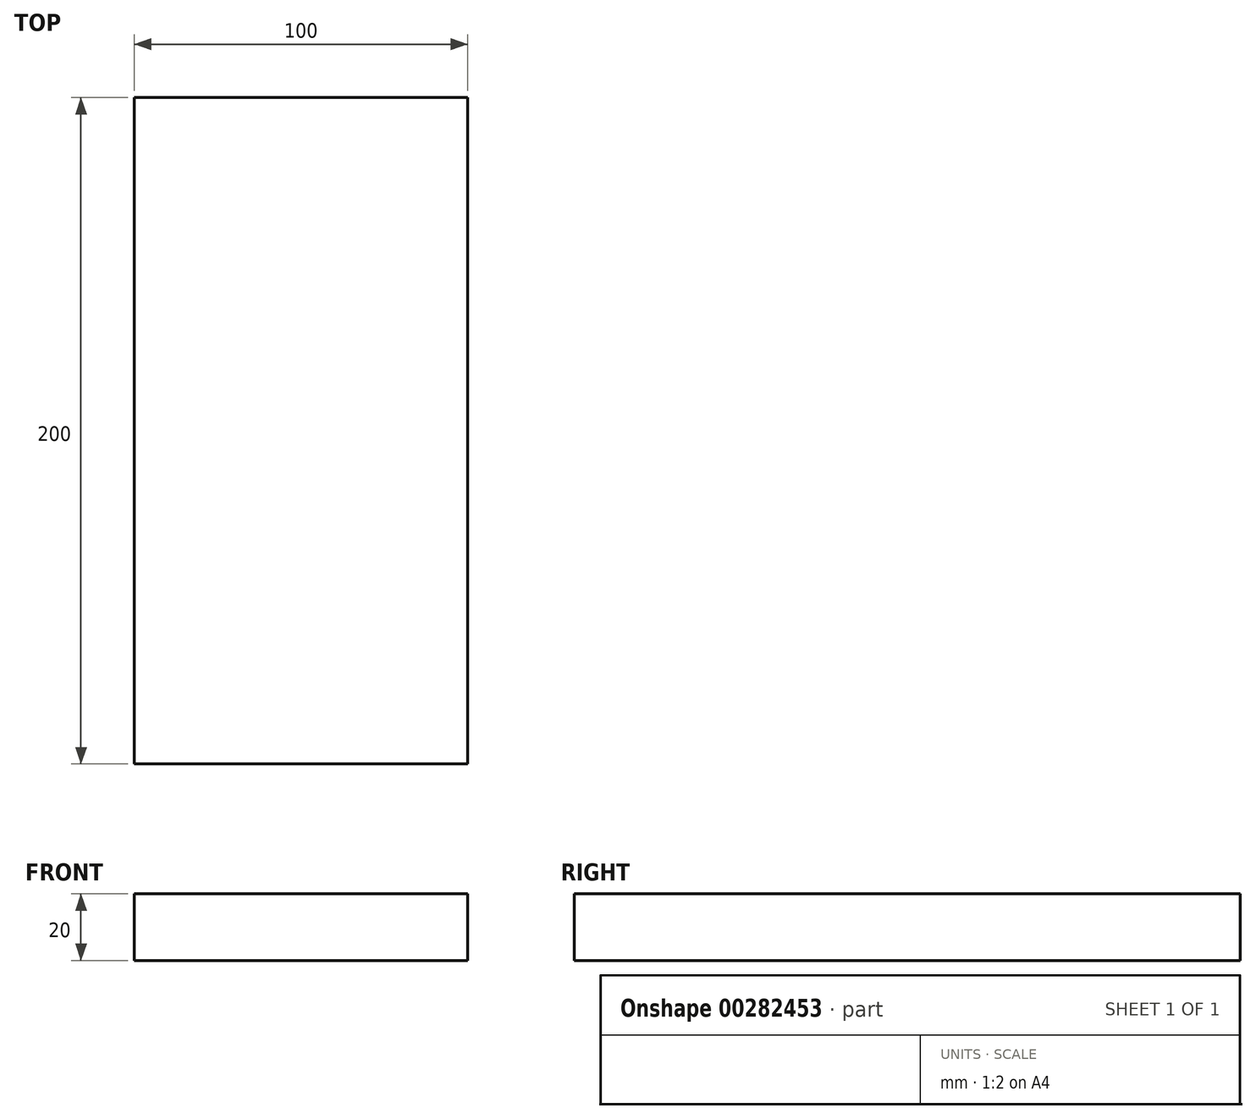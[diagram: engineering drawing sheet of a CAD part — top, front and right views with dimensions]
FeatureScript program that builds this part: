
annotation { "Feature Type Name" : "Feature", "Feature Type Description" : "" }
export const myFeature = defineFeature(function(context is Context, id is Id, definition is map)
    precondition{}
    {
        {
            var Q0;
            Q0=qCreatedBy(makeId("Front.planeOp"),FACE);
            var sketch = newSketch(context, id + "F0", { "sketchPlane" : qUnion([Q0])});
            skLineSegment(sketch, "E0.bottom", {"start": v(-53.91, 0) * mm, "end": v(46.09, 0) * mm});
            skLineSegment(sketch, "E0.top", {"start": v(-53.91, 20) * mm, "end": v(46.09, 20) * mm});
            skLineSegment(sketch, "E0.left", {"start": v(-53.91, 0) * mm, "end": v(-53.91, 20) * mm});
            skLineSegment(sketch, "E0.right", {"start": v(46.09, 0) * mm, "end": v(46.09, 20) * mm});
            skLineSegment(sketch, "E1.bottom", {"start": v(-38.07, 20) * mm, "end": v(30.46, 20) * mm});
            skLineSegment(sketch, "E1.top", {"start": v(-38.07, 30) * mm, "end": v(30.46, 30) * mm});
            skLineSegment(sketch, "E1.left", {"start": v(-38.07, 20) * mm, "end": v(-38.07, 30) * mm});
            skLineSegment(sketch, "E1.right", {"start": v(30.46, 20) * mm, "end": v(30.46, 30) * mm});
            skSolve(sketch);
        }
        {
            var Q0;
            Q0=makeQuery(id+"F0.imprint","IMPRINT",FACE,{"disambiguationData":[TD([[makeQuery(id+"F0.imprint","IMPRINT",EDGE,{"derivedFrom":sQuery(id+"F0.wireOp",EDGE,"E0.bottom")}),1.0]])]});
            var Q1;
            Q1=makeQuery(id+"F0.imprint","IMPRINT",FACE,{"disambiguationData":[TD([[makeQuery(id+"F0.imprint","IMPRINT",EDGE,{"derivedFrom":sQuery(id+"F0.wireOp",EDGE,"E1.bottom")}),1.0]])]});
            extrude(context, id + "F1", {"entities" : qUnion([Q0, Q1]), "depth" : 200 * mm});
        }
    });
